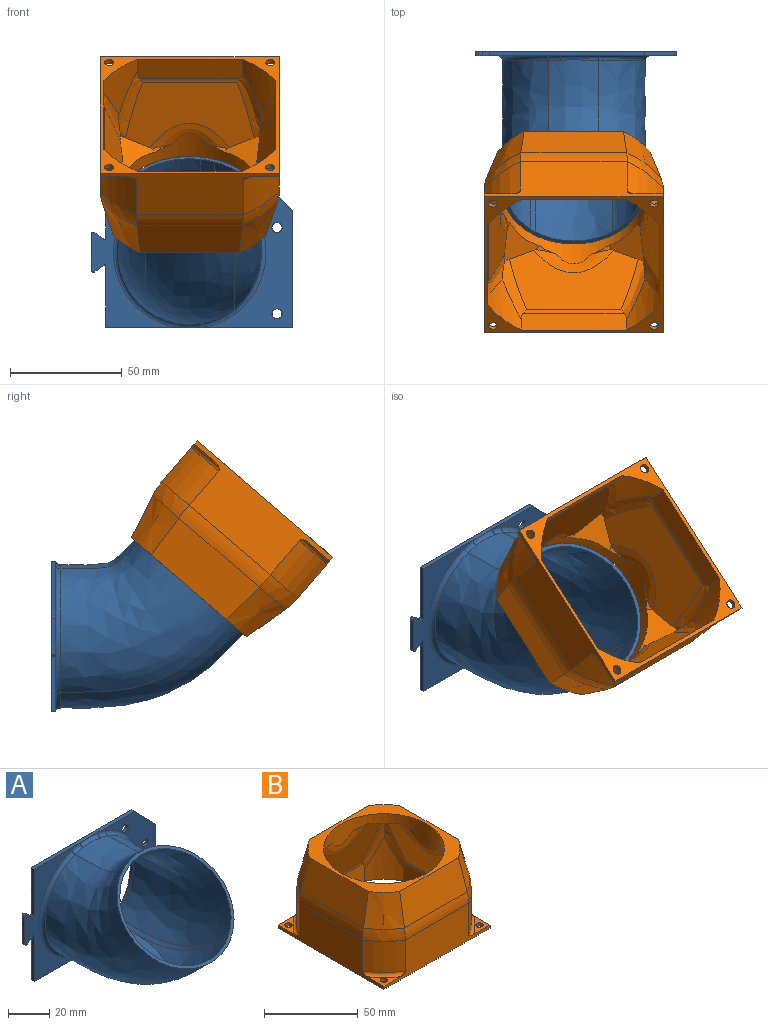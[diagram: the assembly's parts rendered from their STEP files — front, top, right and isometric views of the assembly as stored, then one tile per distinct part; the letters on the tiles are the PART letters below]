
ASSEMBLY  parts=2 mates=1
PART A: 51 faces, bbox 92.6x122.7x81 mm
  f0: plane 68.01x38.71mm, normal (0,-1,0), area 787.8mm2, adj f4,f5,f6,f7,f8,f9,f10,f18
  f1: bspline ~34.66x21.65mm, area 539.9mm2, adj f33,f35,f42
  f2: bspline ~86.21x38.27mm, area 1886.8mm2, adj f26,f33,f35,f41
  f3: plane 67.01x39.7mm, normal (0,-1,0), area 1104mm2, adj f4,f10,f11,f12,f13,f14,f15,f43
  f4: plane 69.05x2.05mm, normal (0,0,1), area 138mm2, adj f0,f3,f5,f14,f17,f46
  f5: plane 24.44x2mm, normal (-1,0,0), area 48.9mm2, adj f0,f4,f17,f21
  f6: plane 2x1.67mm, normal (0.61,0,0.79), area 4.2mm2, adj f0,f17,f18,f21
  f7: plane 15.94x2mm, normal (-1,0,0), area 31.9mm2, adj f0,f17,f18,f19
  f8: plane 2x1.67mm, normal (0.61,0,-0.79), area 4.2mm2, adj f0,f17,f19,f20
  f9: plane 24.44x2mm, normal (-1,0,0), area 48.9mm2, adj f0,f10,f17,f20
  f10: plane 83.55x2.05mm, normal (0,0,-1), area 167mm2, adj f0,f3,f9,f11,f17,f47
  f11: plane 52x2mm, normal (1,0,0), area 104mm2, adj f3,f10,f14,f17
  f12: cylinder r=2.25mm len=4.5mm, axis (0,1,0), area 28.3mm2, adj f3,f17
  f13: cylinder r=2.25mm len=4.5mm, axis (0,1,0), area 28.3mm2, adj f3,f17
  f14: plane 15x14.5mm, normal (0.72,0,0.7), area 41.7mm2, adj f3,f4,f11,f17
  f15: cylinder r=2.25mm len=4.5mm, axis (0,1,0), area 28.3mm2, adj f3,f17
  f16: plane 9.86x0.41mm, normal (0,-1,0), area 2.6mm2, adj f30,f38
  f17: plane 91.01x68.01mm, normal (0,1,0), area 2742.6mm2, adj f4,f5,f6,f7,f8,f9,f10,f11
  f18: cylinder r=1mm len=2mm, axis (0,-1,0), area 4.5mm2, adj f0,f6,f7,f17
  f19: cylinder r=1mm len=2mm, axis (0,1,0), area 4.5mm2, adj f0,f7,f8,f17
  f20: bspline ~3.83x3.22mm, area 13.9mm2, adj f0,f8,f9,f17
  f21: bspline ~3.83x3.22mm, area 13.9mm2, adj f0,f5,f6,f17
  f22: cylinder r=30.5mm len=52mm, axis (0,1,0), area 127.3mm2, adj f17,f24,f33,f36,f39
  f23: cylinder r=30.5mm len=52mm, axis (0,1,0), area 127.2mm2, adj f17,f25,f35,f37,f40
  f24: bspline ~77.51x64.06mm, area 4018.3mm2, adj f22,f26,f33,f39
  f25: bspline ~78.13x64.4mm, area 4018.3mm2, adj f23,f26,f35,f40
  f26: plane 66.77x51.27mm, normal (0,-0.65,0.76), area 314.7mm2, adj f2,f24,f25,f27,f28,f29,f30,f31
  f27: bspline ~77.41x66.71mm, area 4144.2mm2, adj f26,f29,f31,f43
  f28: bspline ~76.88x66.7mm, area 4144.2mm2, adj f26,f29,f31,f50
  f29: bspline ~34.87x22.31mm, area 857.6mm2, adj f26,f27,f28,f44,f46,f48
  f30: bspline ~39.43x12.35mm, area 401mm2, adj f16,f26,f39,f40
  f31: bspline ~87.94x40.56mm, area 3900.6mm2, adj f26,f27,f28,f45,f47,f49
  f32: plane 34.66x0.16mm, normal (0,0,1), area 5.6mm2, adj f17,f34,f36,f37
  f33: bspline ~80.57x31.77mm, area 237.4mm2, adj f1,f2,f22,f24,f26,f34,f36
  f34: bspline ~34.66x21.29mm, area 63.7mm2, adj f32,f33,f35,f41
  f35: bspline ~80.57x31.77mm, area 237.3mm2, adj f1,f2,f23,f25,f26,f34,f37
  f36: bspline ~32.16x2.11mm, area 0.4mm2, adj f17,f22,f32,f33
  f37: bspline ~32.16x2.11mm, area 0.4mm2, adj f17,f23,f32,f35
  f38: bspline ~18.96x9.85mm, area 19.7mm2, adj f16,f17,f39,f40
  f39: bspline ~40.08x13.1mm, area 267.3mm2, adj f17,f22,f24,f26,f30,f38
  f40: bspline ~40.08x13.1mm, area 267.3mm2, adj f17,f23,f25,f26,f30,f38
  f41: plane 46.63x34.66mm, normal (0,0,1), area 1394mm2, adj f2,f34,f42
  f42: extruded ~34.66x14.55mm, area 536.4mm2, adj f1,f41
  f43: bspline ~72.53x36.38mm, area 217.9mm2, adj f3,f27,f44,f45
  f44: bspline ~10.33x4.93mm, area 17.3mm2, adj f3,f29,f43,f46
  f45: bspline ~24.65x14.95mm, area 50mm2, adj f3,f31,f43,f47
  f46: bspline ~14.29x2.21mm, area 33.1mm2, adj f4,f29,f44,f48
  f47: bspline ~14.28x2.18mm, area 34.2mm2, adj f10,f31,f45,f49
  f48: bspline ~13.24x5.32mm, area 17.4mm2, adj f0,f29,f46,f50
  f49: bspline ~24.55x14.94mm, area 50mm2, adj f0,f31,f47,f50
  f50: bspline ~71.95x35.8mm, area 217.8mm2, adj f0,f28,f48,f49
PART B: 79 faces, bbox 94.3x94.3x58.3 mm
  f0: plane 47.4x12.11mm, normal (1,0,0), area 543.2mm2, adj f4,f5,f16,f42,f44,f46
  f1: plane 47.4x12.11mm, normal (0,-1,0), area 543.2mm2, adj f5,f6,f16,f39,f40,f41
  f2: plane 47.4x12.11mm, normal (-1,0,0), area 543.2mm2, adj f6,f7,f16,f43,f45,f47
  f3: plane 47.4x12.1mm, normal (0,1,0), area 543.2mm2, adj f4,f7,f16,f48,f49,f50
  f4: cylinder r=45mm len=27.44mm, axis (0,0,-1), area 369.8mm2, adj f0,f3,f16,f46,f48
  f5: cylinder r=45mm len=27.44mm, axis (0,0,-1), area 369.8mm2, adj f0,f1,f16,f40,f42
  f6: cylinder r=45mm len=27.44mm, axis (0,0,-1), area 369.8mm2, adj f1,f2,f16,f41,f43
  f7: cylinder r=45mm len=27.44mm, axis (0,0,-1), area 369.8mm2, adj f2,f3,f16,f47,f49
  f8: plane 12.4x12.4mm, normal (0,0,1), area 54.9mm2, adj f13,f14,f18,f63
  f9: plane 12.4x12.4mm, normal (0,0,1), area 54.9mm2, adj f11,f14,f17,f66
  f10: plane 12.4x12.4mm, normal (0,0,1), area 54.9mm2, adj f12,f13,f19,f64
  f11: plane 80.86x25.11mm, normal (-1,0,0), area 1227.2mm2, adj f9,f12,f14,f15,f16,f21,f24,f65
  f12: plane 80.86x25.11mm, normal (0,-1,0), area 1227.2mm2, adj f10,f11,f13,f15,f16,f21,f22,f64
  f13: plane 80.86x25.11mm, normal (1,0,0), area 1227.2mm2, adj f8,f10,f12,f14,f16,f22,f23,f63
  f14: plane 80.86x25.11mm, normal (0,1,0), area 1227.2mm2, adj f8,f9,f11,f13,f16,f23,f24,f63
  f15: plane 12.4x12.4mm, normal (0,0,1), area 54.9mm2, adj f11,f12,f20,f65
  f16: plane 80x80mm, normal (0,0,-1), area 826.8mm2, adj f0,f1,f2,f3,f4,f5,f6,f7
  f17: cylinder r=2mm len=4mm, axis (0,0,1), area 25.1mm2, adj f9,f16
  f18: cylinder r=2mm len=4mm, axis (0,0,1), area 25.1mm2, adj f8,f16
  f19: cylinder r=2mm len=4mm, axis (0,0,1), area 25.1mm2, adj f10,f16
  f20: cylinder r=2mm len=4mm, axis (0,0,1), area 25.1mm2, adj f15,f16
  f21: cylinder r=46.6mm len=20.25mm, axis (0,0,-1), area 465.6mm2, adj f11,f12,f65,f72
  f22: cylinder r=46.6mm len=20.25mm, axis (0,0,-1), area 465.6mm2, adj f12,f13,f64,f68
  f23: cylinder r=46.6mm len=20.25mm, axis (0,0,-1), area 465.6mm2, adj f13,f14,f63,f69
  f24: cylinder r=46.6mm len=20.25mm, axis (0,0,-1), area 465.6mm2, adj f11,f14,f66,f73
  f25: plane 68x68mm, normal (0,0,1), area 1116.3mm2, adj f26,f55,f56,f57,f58,f59,f60,f61
  f26: cylinder r=32.25mm len=64.5mm, axis (0,0,1), area 1607.3mm2, adj f25,f31,f32,f33,f34,f35,f36,f37
  f27: plane 57.45x31.09mm, normal (0.97,0,-0.26), area 1317.9mm2, adj f42,f44,f46,f54,f77,f78
  f28: plane 57.45x31.09mm, normal (0,0.97,-0.26), area 1317.9mm2, adj f48,f49,f50,f51,f76,f77
  f29: plane 57.45x31.09mm, normal (0,-0.97,-0.26), area 1317.9mm2, adj f39,f40,f41,f53,f75,f78
  f30: plane 57.45x31.09mm, normal (-0.97,0,-0.26), area 1317.9mm2, adj f43,f45,f47,f52,f75,f76
  f31: plane 9.63x3.43mm, normal (0,-0.61,-0.79), area 6.2mm2, adj f26,f53,f78
  f32: plane 9.63x3.43mm, normal (0.61,0,-0.79), area 6.2mm2, adj f26,f54,f78
  f33: plane 9.63x3.43mm, normal (-0.61,0,-0.79), area 6.2mm2, adj f26,f52,f75
  f34: plane 9.63x3.43mm, normal (0,-0.61,-0.79), area 6.2mm2, adj f26,f53,f75
  f35: plane 9.63x3.43mm, normal (0,0.61,-0.79), area 6.2mm2, adj f26,f51,f76
  f36: plane 9.63x3.43mm, normal (-0.61,0,-0.79), area 6.2mm2, adj f26,f52,f76
  f37: plane 9.63x3.43mm, normal (0,0.61,-0.79), area 6.2mm2, adj f26,f51,f77
  f38: plane 9.63x3.43mm, normal (0.61,0,-0.79), area 6.2mm2, adj f26,f54,f77
  f39: cylinder r=8mm len=45.04mm, axis (-1,0,0), area 91.3mm2, adj f1,f29,f40,f41
  f40: bspline ~32.88x15.65mm, area 164.8mm2, adj f1,f5,f29,f39,f42,f78
  f41: bspline ~32.88x15.65mm, area 164.8mm2, adj f1,f6,f29,f39,f43,f75
  f42: bspline ~32.88x15.65mm, area 164.8mm2, adj f0,f5,f27,f40,f44,f78
  f43: bspline ~32.88x15.65mm, area 164.8mm2, adj f2,f6,f30,f41,f45,f75
  f44: cylinder r=8mm len=45.04mm, axis (0,-1,0), area 91.3mm2, adj f0,f27,f42,f46
  f45: cylinder r=8mm len=45.04mm, axis (0,1,0), area 91.3mm2, adj f2,f30,f43,f47
  f46: bspline ~32.88x15.65mm, area 164.8mm2, adj f0,f4,f27,f44,f48,f77
  f47: bspline ~32.88x15.65mm, area 164.8mm2, adj f2,f7,f30,f45,f49,f76
  f48: bspline ~32.88x15.65mm, area 164.8mm2, adj f3,f4,f28,f46,f50,f77
  f49: bspline ~32.88x15.65mm, area 164.8mm2, adj f3,f7,f28,f47,f50,f76
  f50: cylinder r=8mm len=45.04mm, axis (1,0,0), area 91.3mm2, adj f3,f28,f48,f49
  f51: bspline ~44.35x23.89mm, area 209.8mm2, adj f26,f28,f35,f37,f76,f77
  f52: bspline ~44.35x23.89mm, area 209.8mm2, adj f26,f30,f33,f36,f75,f76
  f53: bspline ~44.35x23.89mm, area 209.8mm2, adj f26,f29,f31,f34,f75,f78
  f54: bspline ~44.35x23.89mm, area 209.8mm2, adj f26,f27,f32,f38,f77,f78
  f55: plane 47.39x20.56mm, normal (-0.97,0,0.24), area 968.6mm2, adj f25,f56,f57,f74
  f56: cone r=40.6mm half-angle=14deg, axis (0,0,-1), area 409.4mm2, adj f25,f55,f58,f72
  f57: cone r=40.6mm half-angle=14deg, axis (0,0,-1), area 409.4mm2, adj f25,f55,f59,f73
  f58: plane 47.39x20.56mm, normal (0,-0.97,0.24), area 968.6mm2, adj f25,f56,f60,f70
  f59: plane 47.39x20.56mm, normal (0,0.97,0.24), area 968.6mm2, adj f25,f57,f61,f71
  f60: cone r=40.6mm half-angle=14deg, axis (0,0,-1), area 409.4mm2, adj f25,f58,f62,f68
  f61: cone r=46.6mm half-angle=14deg, axis (0,0,-1), area 409.4mm2, adj f25,f59,f62,f69
  f62: plane 47.39x20.56mm, normal (0.97,0,0.24), area 968.6mm2, adj f25,f60,f61,f67
  f63: torus R=48.6mm, axis (0,0,1), area 63.6mm2, adj f8,f13,f14,f23
  f64: torus R=48.6mm, axis (0,0,1), area 63.6mm2, adj f10,f12,f13,f22
  f65: torus R=48.6mm, axis (0,0,1), area 63.6mm2, adj f11,f12,f15,f21
  f66: torus R=48.6mm, axis (0,0,1), area 63.6mm2, adj f9,f11,f14,f24
  f67: cylinder r=30mm len=47.81mm, axis (0,1,0), area 348.7mm2, adj f13,f62,f68,f69
  f68: torus R=16.6mm, axis (0,0,1), area 165.6mm2, adj f22,f60,f67,f70
  f69: torus R=16.6mm, axis (0,0,1), area 165.6mm2, adj f23,f61,f67,f71
  f70: cylinder r=30mm len=47.81mm, axis (1,0,0), area 348.7mm2, adj f12,f58,f68,f72
  f71: cylinder r=30mm len=47.81mm, axis (-1,0,0), area 348.7mm2, adj f14,f59,f69,f73
  f72: torus R=16.6mm, axis (0,0,1), area 165.6mm2, adj f21,f56,f70,f74
  f73: torus R=16.6mm, axis (0,0,1), area 165.6mm2, adj f24,f57,f71,f74
  f74: cylinder r=30mm len=47.81mm, axis (0,-1,0), area 348.7mm2, adj f11,f55,f72,f73
  f75: plane 16.98x16.98mm, normal (-0.34,-0.34,-0.88), area 139.4mm2, adj f26,f29,f30,f33,f34,f41,f43,f52
  f76: plane 16.98x16.98mm, normal (-0.34,0.34,-0.88), area 139.4mm2, adj f26,f28,f30,f35,f36,f47,f49,f51
  f77: plane 16.98x16.98mm, normal (0.34,0.34,-0.88), area 139.4mm2, adj f26,f27,f28,f37,f38,f46,f48,f51
  f78: plane 16.98x16.98mm, normal (0.34,-0.34,-0.88), area 139.4mm2, adj f26,f27,f29,f31,f32,f40,f42,f53
PLACE A t=(-68.13,-5.53,-8.79)mm fixed
PLACE B rot(axis=(-1,0,0),139.3deg) t=(-108.13,-70.76,78.64)mm
MATE cylindrical B.f4 <-> A.f26  axis (0,0.65,-0.76) through (-68.13,-67.21,13.13)mm
